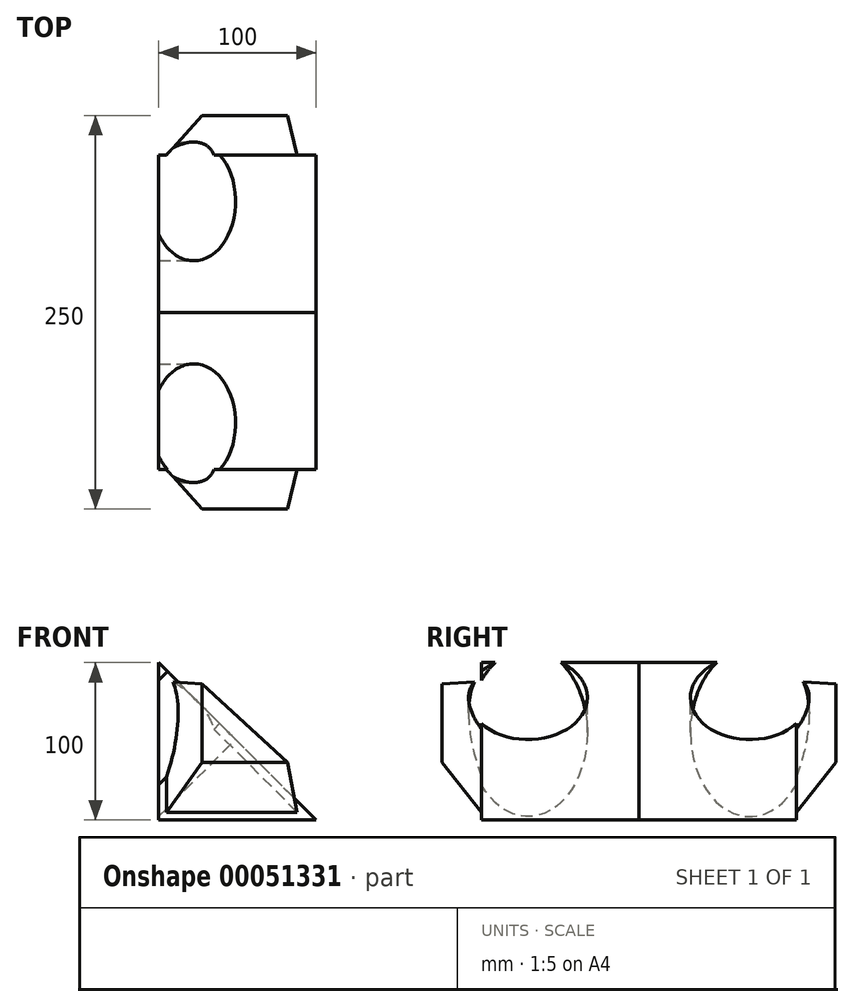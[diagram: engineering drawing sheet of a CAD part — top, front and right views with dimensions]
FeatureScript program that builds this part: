
annotation { "Feature Type Name" : "Feature", "Feature Type Description" : "" }
export const myFeature = defineFeature(function(context is Context, id is Id, definition is map)
    precondition{}
    {
        {
            var Q0;
            Q0=qCreatedBy(makeId("Front.planeOp"),FACE);
            var sketch = newSketch(context, id + "F0", { "sketchPlane" : qUnion([Q0])});
            skLineSegment(sketch, "E0", {"start": v(0, 0) * mm, "end": v(0, 100) * mm});
            skLineSegment(sketch, "E1", {"start": v(0, 100) * mm, "end": v(100, 0) * mm});
            skLineSegment(sketch, "E2", {"start": v(100, 0) * mm, "end": v(0, 0) * mm});
            skSolve(sketch);
        }
        {
            var Q0;
            Q0 = qSketchRegion(id + "F0", true);
            extrude(context, id + "F1", {"entities" : qUnion([Q0]), "depth" : 100 * mm});
        }
        {
            var Q0;
            Q0=makeQuery(id+"F1.opExtrude","CAP_FACE",FACE,{"disambiguationData":[OSD([sQuery(id+"F0.wireOp",EDGE,"E0"),sQuery(id+"F0.wireOp",EDGE,"E1"),sQuery(id+"F0.wireOp",EDGE,"E2")])],"isStart":false});
            cPlane(context, id + "F2", {"entities" : qUnion([Q0]), "cplaneType" : CPlaneType.OFFSET, "offset" : 25 * mm, "width" : 150 * mm, "height" : 150 * mm});
        }
        {
            var Q0;
            Q0=qCreatedBy(id+"F2.planeOp",FACE);
            var sketch = newSketch(context, id + "F3", { "sketchPlane" : qUnion([Q0])});
            skLineSegment(sketch, "E3", {"start": v(27.6, 86.51) * mm, "end": v(27.6, 36.68) * mm});
            skLineSegment(sketch, "E4", {"start": v(27.6, 36.68) * mm, "end": v(81.73, 36.68) * mm});
            skLineSegment(sketch, "E5", {"start": v(81.73, 36.68) * mm, "end": v(27.6, 86.51) * mm});
            skSolve(sketch);
        }
        {
            var Q0;
            Q0=makeQuery(id+"F1.opExtrude","CAP_FACE",FACE,{"disambiguationData":[OSD([sQuery(id+"F0.wireOp",EDGE,"E0"),sQuery(id+"F0.wireOp",EDGE,"E1"),sQuery(id+"F0.wireOp",EDGE,"E2")])],"isStart":false});
            var sketch = newSketch(context, id + "F4", { "sketchPlane" : qUnion([Q0])});
            skLineSegment(sketch, "E6.0", {"start": v(5, 87.93) * mm, "end": v(5, 5) * mm});
            skLineSegment(sketch, "E6.1", {"start": v(87.93, 5) * mm, "end": v(5, 87.93) * mm});
            skLineSegment(sketch, "E6.2", {"start": v(5, 5) * mm, "end": v(87.93, 5) * mm});
            skSolve(sketch);
        }
        {
            var Q1;
            Q1 = qSketchRegion(id + "F3", true);
            var Q2;
            Q2 = qSketchRegion(id + "F4", true);
            loft(context, id + "F5", {"operationType" : NewBodyOperationType.ADD, "sheetProfilesArray" : [{ "sheetProfileEntities" : qUnion([Q1]) }, { "sheetProfileEntities" : qUnion([Q2]) }]});
        }
        {
            var Q0;
            Q0=makeQuery(id+"F1.opExtrude","SWEPT_FACE",FACE,{"disambiguationData":[OSD([sQuery(id+"F0.wireOp",EDGE,"E1")])]});
            var sketch = newSketch(context, id + "F6", { "sketchPlane" : qUnion([Q0])});
            skCircle(sketch, "E7", {"center": v(-70.44, 39.29) * mm, "radius": 37.71 * mm});
            skSolve(sketch);
        }
        {
            var Q0;
            Q0 = qSketchRegion(id + "F6", true);
            extrude(context, id + "F7", {"entities" : qUnion([Q0]), "operationType" : NewBodyOperationType.REMOVE, "endBound" : BoundingType.THROUGH_ALL, "oppositeDirection" : true, "depth" : 25 * mm});
        }
        {
            var Q0;
            Q0=makeQuery(id+"F7.boolean.opBoolean","SPLIT",BODY,{"disambiguationData":[OD(1.0)],"derivedFrom":makeQuery(id+"F1.opExtrude","SWEPT_BODY",BODY,{"disambiguationData":[OSD([sQuery(id+"F0.wireOp",EDGE,"E0"),sQuery(id+"F0.wireOp",EDGE,"E1"),sQuery(id+"F0.wireOp",EDGE,"E2")])]})});
            var Q1;
            Q1=makeQuery(id+"F1.opExtrude","CAP_FACE",FACE,{"disambiguationData":[OSD([sQuery(id+"F0.wireOp",EDGE,"E0"),sQuery(id+"F0.wireOp",EDGE,"E1"),sQuery(id+"F0.wireOp",EDGE,"E2")])],"isStart":true});
            mirror(context, id + "F8", {"operationType" : NewBodyOperationType.ADD, "entities" : qUnion([Q0]), "mirrorPlane" : qUnion([Q1])});
        }
    });
